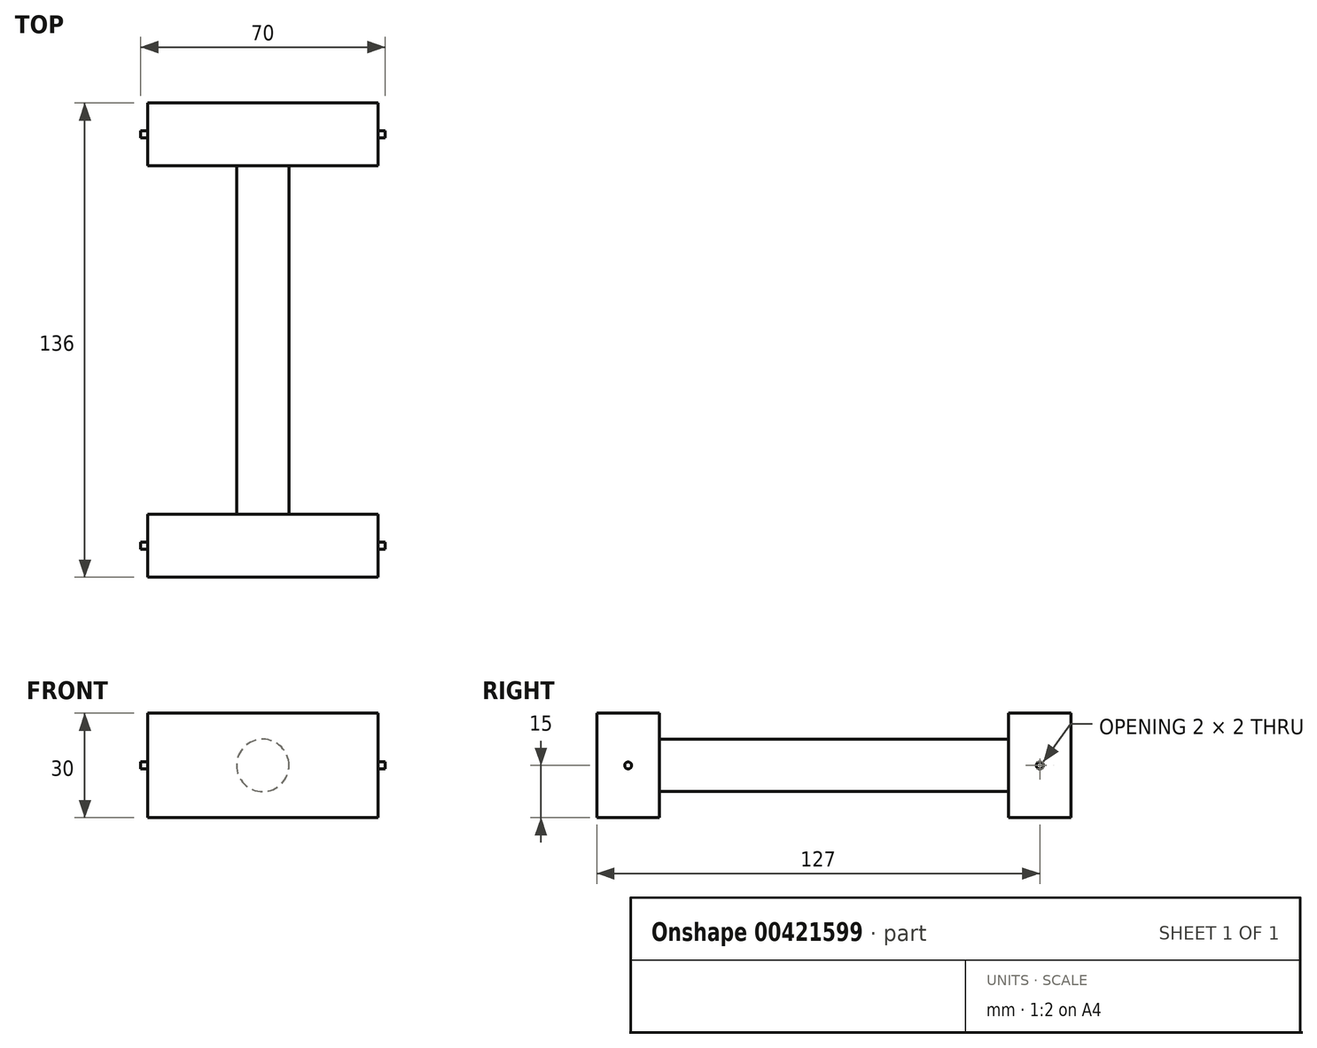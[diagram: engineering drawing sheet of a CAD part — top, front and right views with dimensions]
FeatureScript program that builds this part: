
annotation { "Feature Type Name" : "Feature", "Feature Type Description" : "" }
export const myFeature = defineFeature(function(context is Context, id is Id, definition is map)
    precondition{}
    {
        {
            var Q0;
            Q0=qCreatedBy(makeId("Front.planeOp"),FACE);
            var sketch = newSketch(context, id + "F0", { "sketchPlane" : qUnion([Q0])});
            skLineSegment(sketch, "E0.bottom", {"start": v(33, 15) * mm, "end": v(-33, 15) * mm});
            skLineSegment(sketch, "E0.top", {"start": v(33, -15) * mm, "end": v(-33, -15) * mm});
            skLineSegment(sketch, "E0.left", {"start": v(33, 15) * mm, "end": v(33, -15) * mm});
            skLineSegment(sketch, "E0.right", {"start": v(-33, 15) * mm, "end": v(-33, -15) * mm});
            skPoint(sketch, "E0.middle", {"position": v(0, 0) * mm});
            skCircle(sketch, "E1", {"center": v(0, 0) * mm, "radius": 7.5 * mm});
            skSolve(sketch);
        }
        {
            var Q0;
            Q0=makeQuery(id+"F0.imprint","IMPRINT",FACE,{"disambiguationData":[TD([[makeQuery(id+"F0.imprint","IMPRINT",EDGE,{"derivedFrom":sQuery(id+"F0.wireOp",EDGE,"E0.bottom")}),1.0]])]});
            var Q1;
            Q1=makeQuery(id+"F0.imprint","IMPRINT",FACE,{"disambiguationData":[TD([[makeQuery(id+"F0.imprint","IMPRINT",EDGE,{"derivedFrom":sQuery(id+"F0.wireOp",EDGE,"E1")}),1.0]])]});
            extrude(context, id + "F1", {"entities" : qUnion([Q0, Q1]), "depth" : 18 * mm});
        }
        {
            var Q0;
            Q0=makeQuery(id+"F1.opExtrude","SWEPT_FACE",FACE,{"disambiguationData":[OSD([sQuery(id+"F0.wireOp",EDGE,"E0.left")])]});
            cPlane(context, id + "F2", {"entities" : qUnion([Q0]), "cplaneType" : CPlaneType.OFFSET, "offset" : 2 * mm, "width" : 150 * mm, "height" : 150 * mm});
        }
        {
            var Q0;
            Q0=qCreatedBy(id+"F2.planeOp",FACE);
            var sketch = newSketch(context, id + "F3", { "sketchPlane" : qUnion([Q0])});
            skCircle(sketch, "E2", {"center": v(-9, 0) * mm, "radius": 1 * mm});
            skSolve(sketch);
        }
        {
            var Q0;
            Q0=makeQuery(id+"F3.imprint","IMPRINT",FACE,{"disambiguationData":[TD([[makeQuery(id+"F3.imprint","IMPRINT",EDGE,{"derivedFrom":sQuery(id+"F3.wireOp",EDGE,"E2")}),1.0]])]});
            extrude(context, id + "F4", {"entities" : qUnion([Q0]), "operationType" : NewBodyOperationType.ADD, "oppositeDirection" : true, "depth" : 70 * mm});
        }
        {
            var Q0;
            Q0=makeQuery(id+"F0.imprint","IMPRINT",FACE,{"disambiguationData":[TD([[makeQuery(id+"F0.imprint","IMPRINT",EDGE,{"derivedFrom":sQuery(id+"F0.wireOp",EDGE,"E1")}),1.0]])]});
            extrude(context, id + "F5", {"entities" : qUnion([Q0]), "operationType" : NewBodyOperationType.ADD, "oppositeDirection" : true, "depth" : 100 * mm});
        }
        {
            var Q0;
            Q0=makeQuery(id+"F5.opExtrude","CAP_FACE",FACE,{"disambiguationData":[OSD([sQuery(id+"F0.wireOp",EDGE,"E1")])],"isStart":false});
            var sketch = newSketch(context, id + "F6", { "sketchPlane" : qUnion([Q0])});
            skLineSegment(sketch, "E3.bottom", {"start": v(33, 15) * mm, "end": v(-33, 15) * mm});
            skLineSegment(sketch, "E3.top", {"start": v(33, -15) * mm, "end": v(-33, -15) * mm});
            skLineSegment(sketch, "E3.left", {"start": v(33, 15) * mm, "end": v(33, -15) * mm});
            skLineSegment(sketch, "E3.right", {"start": v(-33, 15) * mm, "end": v(-33, -15) * mm});
            skPoint(sketch, "E3.middle", {"position": v(0, 0) * mm});
            skSolve(sketch);
        }
        {
            var Q0;
            Q0=makeQuery(id+"F6.imprint","IMPRINT",FACE,{"disambiguationData":[TD([[makeQuery(id+"F6.imprint","IMPRINT",EDGE,{"derivedFrom":sQuery(id+"F6.wireOp",EDGE,"E3.bottom")}),1.0]])]});
            var Q1;
            Q1=makeQuery(id+"F6.imprint","IMPRINT",FACE,{"disambiguationData":[TD([[makeQuery(id+"F6.imprint","IMPRINT",EDGE,{"derivedFrom":makeQuery(id+"F5.opExtrude","CAP_EDGE",EDGE,{"disambiguationData":[OSD([sQuery(id+"F0.wireOp",EDGE,"E1")])],"isStart":false})}),-1.0]])]});
            extrude(context, id + "F7", {"entities" : qUnion([Q0, Q1]), "operationType" : NewBodyOperationType.ADD, "depth" : 18 * mm});
        }
        {
            var Q0;
            Q0=qCreatedBy(id+"F2.planeOp",FACE);
            var sketch = newSketch(context, id + "F8", { "sketchPlane" : qUnion([Q0])});
            skCircle(sketch, "E4", {"center": v(109, 0) * mm, "radius": 1 * mm});
            skSolve(sketch);
        }
        {
            var Q0;
            Q0=makeQuery(id+"F8.imprint","IMPRINT",FACE,{"disambiguationData":[TD([[makeQuery(id+"F8.imprint","IMPRINT",EDGE,{"derivedFrom":sQuery(id+"F8.wireOp",EDGE,"EkVITYJt-1mNv-F9GY-3z9t-ywBhRBqZZZmZ")}),1.0]])]});
            var Q1;
            Q1=makeQuery(id+"F8.imprint","IMPRINT",FACE,{"disambiguationData":[TD([[makeQuery(id+"F8.imprint","IMPRINT",EDGE,{"derivedFrom":sQuery(id+"F8.wireOp",EDGE,"E4")}),1.0]])]});
            extrude(context, id + "F9", {"entities" : qUnion([Q0, Q1]), "operationType" : NewBodyOperationType.ADD, "oppositeDirection" : true, "depth" : 70 * mm});
        }
    });
